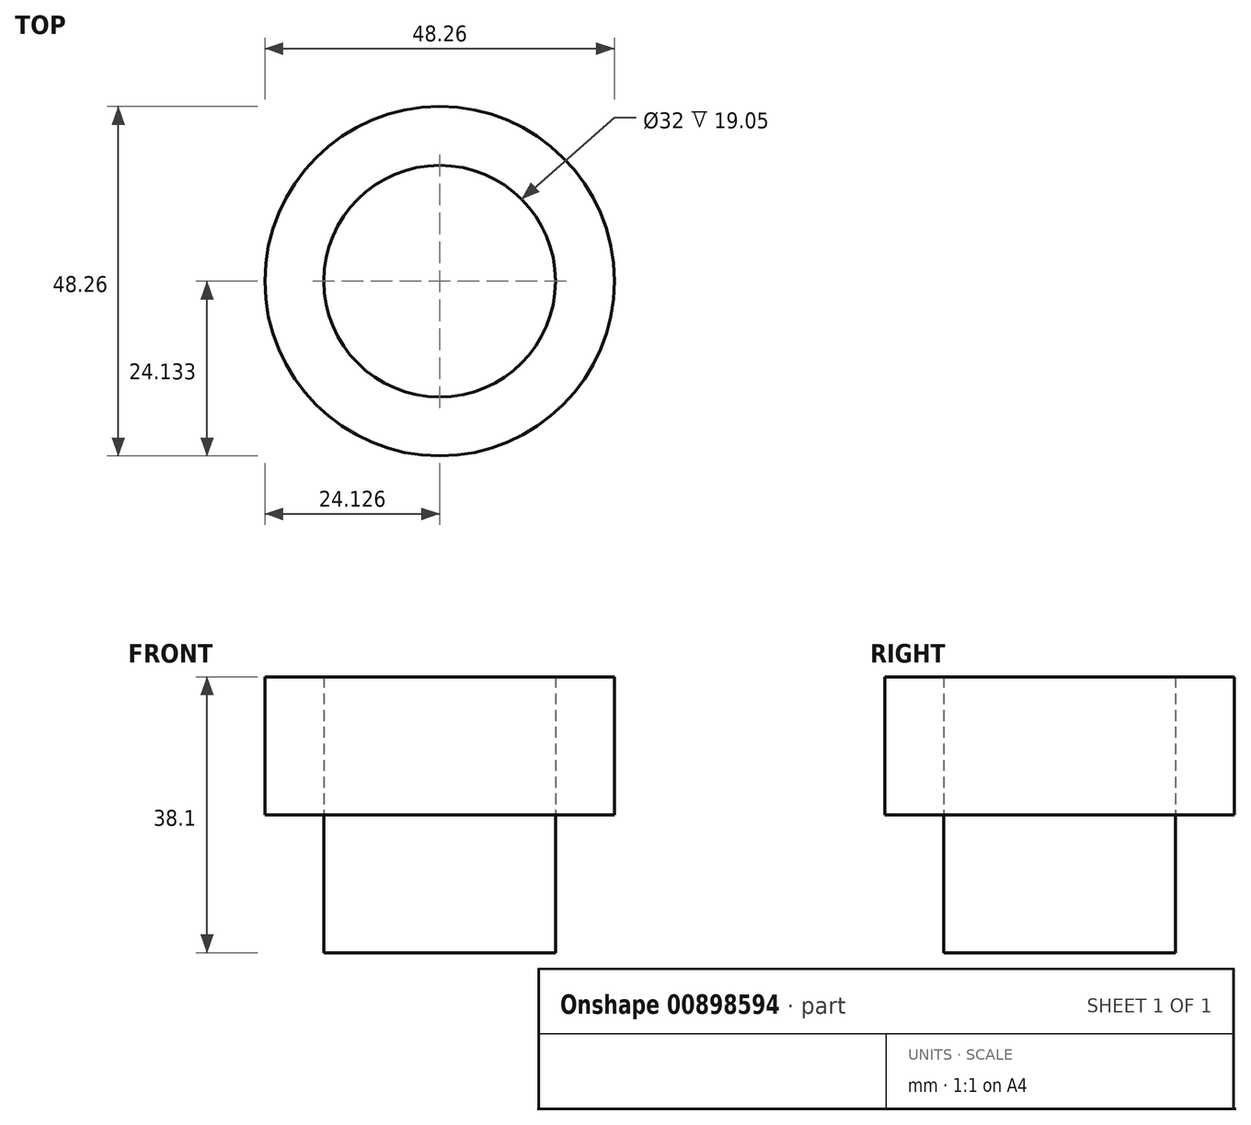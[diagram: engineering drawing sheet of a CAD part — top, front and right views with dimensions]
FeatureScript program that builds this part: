
annotation { "Feature Type Name" : "Feature", "Feature Type Description" : "" }
export const myFeature = defineFeature(function(context is Context, id is Id, definition is map)
    precondition{}
    {
        {
            var Q0;
            Q0=qCreatedBy(makeId("Top.planeOp"),FACE);
            var sketch = newSketch(context, id + "F0", { "sketchPlane" : qUnion([Q0])});
            skCircle(sketch, "E0", {"center": v(-4.22, 14.48) * mm, "radius": 16 * mm});
            skCircle(sketch, "E1", {"center": v(-4.22, 14.48) * mm, "radius": 19.05 * mm});
            skSolve(sketch);
        }
        {
            var Q0;
            Q0=makeQuery(id+"F0.imprint","IMPRINT",FACE,{"disambiguationData":[TD([[makeQuery(id+"F0.imprint","IMPRINT",EDGE,{"derivedFrom":sQuery(id+"F0.wireOp",EDGE,"E0")}),1.0]])]});
            extrude(context, id + "F1", {"entities" : qUnion([Q0]), "depth" : 19.05 * mm, "offsetDistance" : 25.4 * mm});
        }
        {
            var Q0;
            Q0=makeQuery(id+"F1.opExtrude","CAP_FACE",FACE,{"disambiguationData":[OSD([sQuery(id+"F0.wireOp",EDGE,"E0")])],"isStart":false});
            var sketch = newSketch(context, id + "F2", { "sketchPlane" : qUnion([Q0])});
            skCircle(sketch, "E2", {"center": v(-4.22, 14.48) * mm, "radius": 24.13 * mm});
            skSolve(sketch);
        }
        {
            var Q0;
            Q0=makeQuery(id+"F2.imprint","IMPRINT",FACE,{"disambiguationData":[TD([[makeQuery(id+"F2.imprint","IMPRINT",EDGE,{"derivedFrom":sQuery(id+"F2.wireOp",EDGE,"E2")}),1.0]])]});
            extrude(context, id + "F3", {"entities" : qUnion([Q0]), "depth" : 19.05 * mm, "offsetDistance" : 25.4 * mm});
        }
    });
